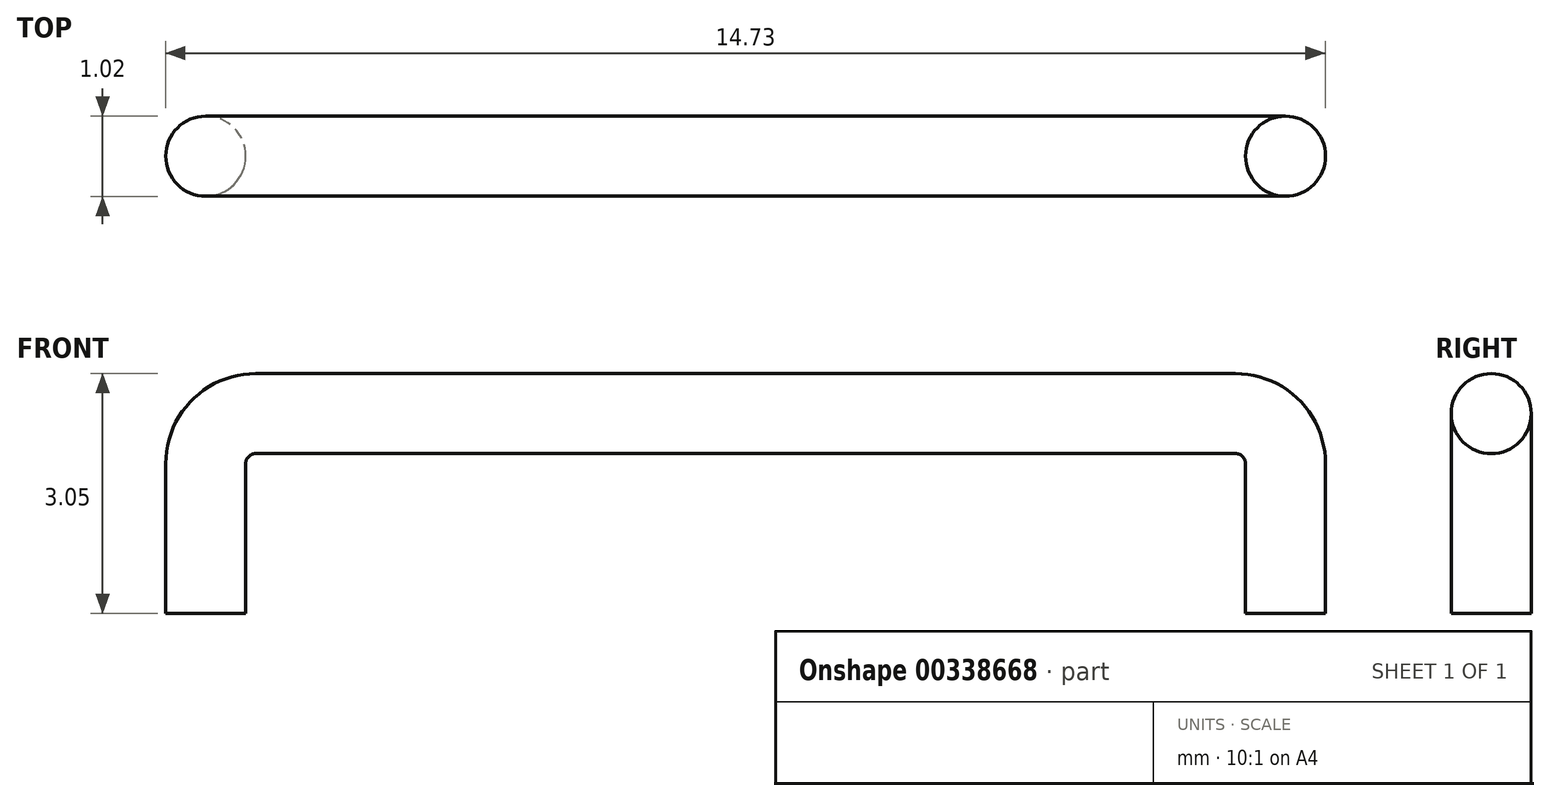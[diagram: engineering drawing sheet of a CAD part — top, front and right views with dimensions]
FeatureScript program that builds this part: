
annotation { "Feature Type Name" : "Feature", "Feature Type Description" : "" }
export const myFeature = defineFeature(function(context is Context, id is Id, definition is map)
    precondition{}
    {
        {
            var Q0;
            Q0=qCreatedBy(makeId("Front.planeOp"),FACE);
            var sketch = newSketch(context, id + "F0", { "sketchPlane" : qUnion([Q0])});
            skLineSegment(sketch, "E0", {"start": v(0, 0) * mm, "end": v(0, 1.9) * mm});
            skLineSegment(sketch, "E1", {"start": v(0.64, 2.54) * mm, "end": v(13.08, 2.54) * mm});
            skLineSegment(sketch, "E2", {"start": v(13.72, 1.9) * mm, "end": v(13.72, 0) * mm});
            skPoint(sketch, "E3.visualSharp", {"position": v(0, 2.54) * mm});
            skArc(sketch, "E3.filletArc", {"start": v(0.64, 2.54) * mm, "mid": v(0.19, 2.35) * mm, "end": v(0, 1.9) * mm});
            skPoint(sketch, "E4.visualSharp", {"position": v(13.72, 2.54) * mm});
            skArc(sketch, "E4.filletArc", {"start": v(13.72, 1.9) * mm, "mid": v(13.53, 2.35) * mm, "end": v(13.08, 2.54) * mm});
            skSolve(sketch);
        }
        {
            var Q0;
            Q0=qCreatedBy(makeId("Top.planeOp"),FACE);
            var sketch = newSketch(context, id + "F1", { "sketchPlane" : qUnion([Q0])});
            skCircle(sketch, "E5", {"center": v(0, 0) * mm, "radius": 0.5 * mm});
            skSolve(sketch);
        }
        {
            var Q0;
            Q0 = qSketchRegion(id + "F1", true);
            var Q1;
            Q1 = qConstructionFilter(qBodyType(qCreatedBy(id + "F0" ,EDGE), BodyType.WIRE), ConstructionObject.NO);
            sweep(context, id + "F2", {"profiles" : qUnion([Q0]), "path" : qUnion([Q1])});
        }
    });
